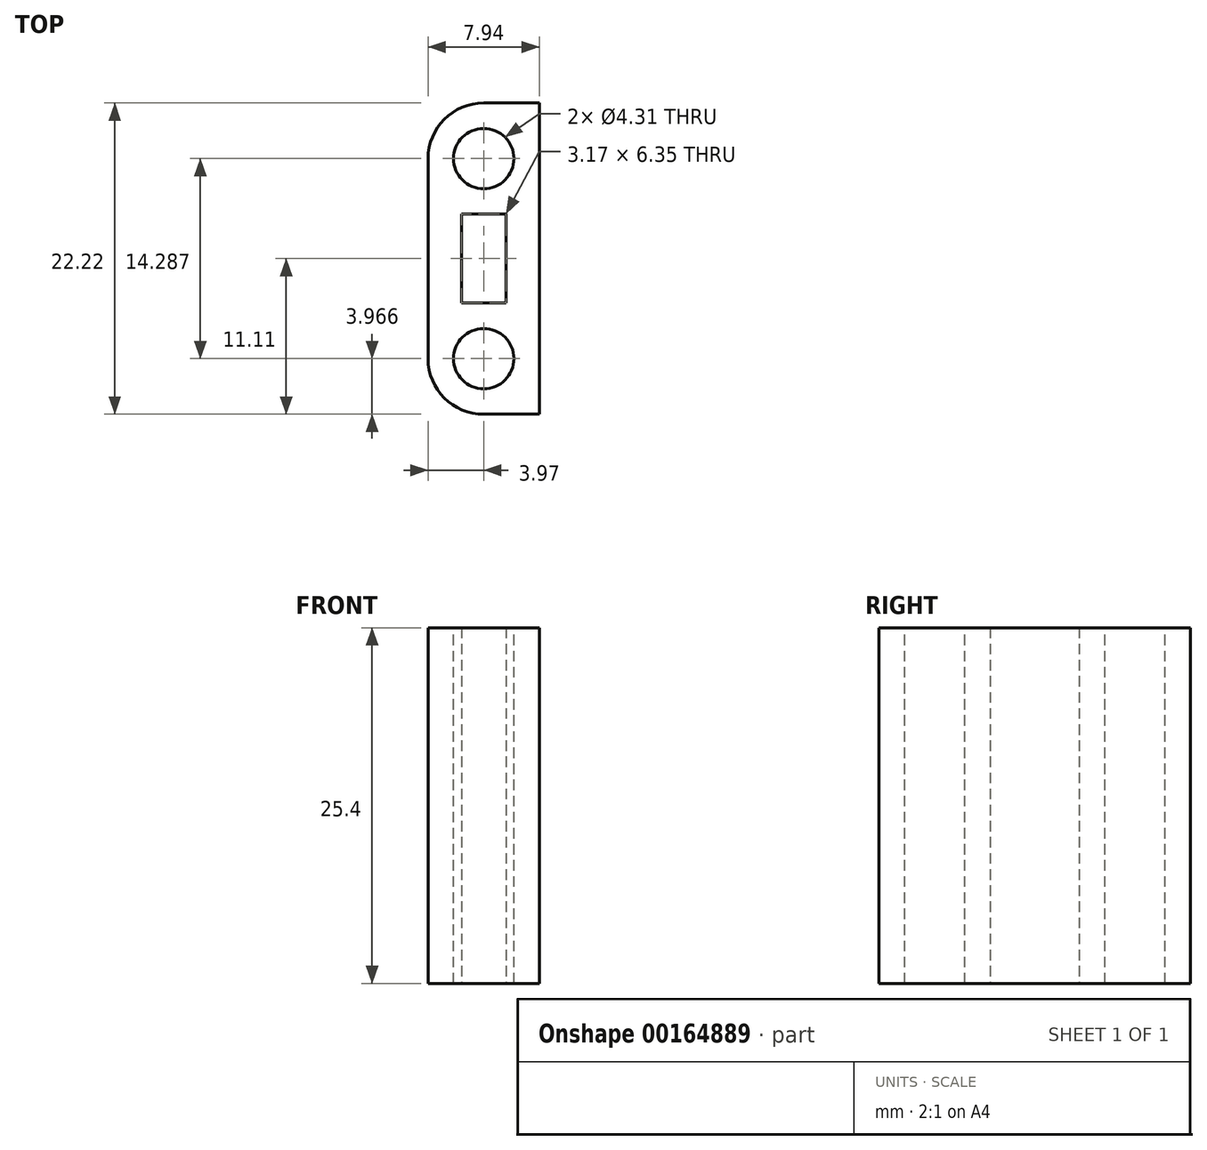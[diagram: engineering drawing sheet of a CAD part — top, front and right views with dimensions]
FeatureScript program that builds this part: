
annotation { "Feature Type Name" : "Feature", "Feature Type Description" : "" }
export const myFeature = defineFeature(function(context is Context, id is Id, definition is map)
    precondition{}
    {
        {
            var Q0;
            Q0=qCreatedBy(makeId("Top.planeOp"),FACE);
            var sketch = newSketch(context, id + "F0", { "sketchPlane" : qUnion([Q0])});
            skLineSegment(sketch, "E0.bottom", {"start": v(3.97, 11.11) * mm, "end": v(-3.97, 11.11) * mm});
            skLineSegment(sketch, "E0.top", {"start": v(3.97, -11.11) * mm, "end": v(-3.97, -11.11) * mm});
            skLineSegment(sketch, "E0.left", {"start": v(3.97, 11.11) * mm, "end": v(3.97, -11.11) * mm});
            skLineSegment(sketch, "E0.right", {"start": v(-3.97, 11.11) * mm, "end": v(-3.97, -11.11) * mm});
            skPoint(sketch, "E0.middle", {"position": v(0, 0) * mm});
            skLineSegment(sketch, "E1.bottom", {"start": v(1.59, 3.18) * mm, "end": v(-1.59, 3.18) * mm});
            skLineSegment(sketch, "E1.top", {"start": v(1.59, -3.18) * mm, "end": v(-1.59, -3.18) * mm});
            skLineSegment(sketch, "E1.left", {"start": v(1.59, 3.18) * mm, "end": v(1.59, -3.18) * mm});
            skLineSegment(sketch, "E1.right", {"start": v(-1.59, 3.18) * mm, "end": v(-1.59, -3.18) * mm});
            skSolve(sketch);
        }
        {
            var Q0;
            Q0=qSketchRegion(id+"F0",true);
            extrude(context, id + "F1", {"entities" : qUnion([Q0]), "depth" : 25.4 * mm});
        }
        {
            var Q0;
            Q0=makeQuery(id+"F1.opExtrude","CAP_FACE",FACE,{"disambiguationData":[OSD([sQuery(id+"F0.wireOp",EDGE,"E0.bottom"),sQuery(id+"F0.wireOp",EDGE,"E0.top"),sQuery(id+"F0.wireOp",EDGE,"E0.left"),sQuery(id+"F0.wireOp",EDGE,"E0.right"),sQuery(id+"F0.wireOp",EDGE,"E1.bottom"),sQuery(id+"F0.wireOp",EDGE,"E1.top"),sQuery(id+"F0.wireOp",EDGE,"E1.left"),sQuery(id+"F0.wireOp",EDGE,"E1.right")])],"isStart":false});
            var sketch = newSketch(context, id + "F2", { "sketchPlane" : qUnion([Q0])});
            skLineSegment(sketch, "E2.bottom", {"start": v(0, 11.11) * mm, "end": v(3.97, 11.11) * mm, "construction": true});
            skLineSegment(sketch, "E2.top", {"start": v(0, 7.14) * mm, "end": v(3.97, 7.14) * mm, "construction": true});
            skLineSegment(sketch, "E2.left", {"start": v(0, 11.11) * mm, "end": v(0, 7.14) * mm, "construction": true});
            skLineSegment(sketch, "E2.right", {"start": v(3.97, 11.11) * mm, "end": v(3.97, 7.14) * mm, "construction": true});
            skLineSegment(sketch, "E3.bottom", {"start": v(0, -11.11) * mm, "end": v(3.97, -11.11) * mm, "construction": true});
            skLineSegment(sketch, "E3.top", {"start": v(0, -7.14) * mm, "end": v(3.97, -7.14) * mm, "construction": true});
            skLineSegment(sketch, "E3.left", {"start": v(0, -11.11) * mm, "end": v(0, -7.14) * mm, "construction": true});
            skLineSegment(sketch, "E3.right", {"start": v(3.97, -11.11) * mm, "end": v(3.97, -7.14) * mm, "construction": true});
            skCircle(sketch, "E4", {"center": v(0, 7.14) * mm, "radius": 2.15 * mm});
            skCircle(sketch, "E5", {"center": v(0, -7.14) * mm, "radius": 2.15 * mm});
            skSolve(sketch);
        }
        {
            var Q0;
            Q0=qSketchRegion(id+"F2",true);
            var Q1;
            Q1=makeQuery(id+"F1.opExtrude","CAP_FACE",FACE,{"disambiguationData":[OSD([sQuery(id+"F0.wireOp",EDGE,"E0.bottom"),sQuery(id+"F0.wireOp",EDGE,"E0.top"),sQuery(id+"F0.wireOp",EDGE,"E0.left"),sQuery(id+"F0.wireOp",EDGE,"E0.right"),sQuery(id+"F0.wireOp",EDGE,"E1.bottom"),sQuery(id+"F0.wireOp",EDGE,"E1.top"),sQuery(id+"F0.wireOp",EDGE,"E1.left"),sQuery(id+"F0.wireOp",EDGE,"E1.right")])],"isStart":true});
            extrude(context, id + "F3", {"entities" : qUnion([Q0]), "operationType" : NewBodyOperationType.REMOVE, "endBound" : BoundingType.UP_TO_SURFACE, "oppositeDirection" : true, "endBoundEntityFace" : qUnion([Q1]), "depth" : 25.4 * mm});
        }
        {
            var Q0;
            Q0=makeQuery(id+"F1.opExtrude","SWEPT_EDGE",EDGE,{"disambiguationData":[OSD([sQuery(id+"F0.wireOp",EDGE,"E0.top"),sQuery(id+"F0.wireOp",EDGE,"E0.right")])]});
            var Q1;
            Q1=makeQuery(id+"F1.opExtrude","SWEPT_EDGE",EDGE,{"disambiguationData":[OSD([sQuery(id+"F0.wireOp",EDGE,"E0.bottom"),sQuery(id+"F0.wireOp",EDGE,"E0.right")])]});
            fillet(context, id + "F4", {"entities" : qUnion([Q0, Q1]), "radius" : 3.97 * mm, "tangentPropagation" : true, "allowEdgeOverflow" : false});
        }
    });
